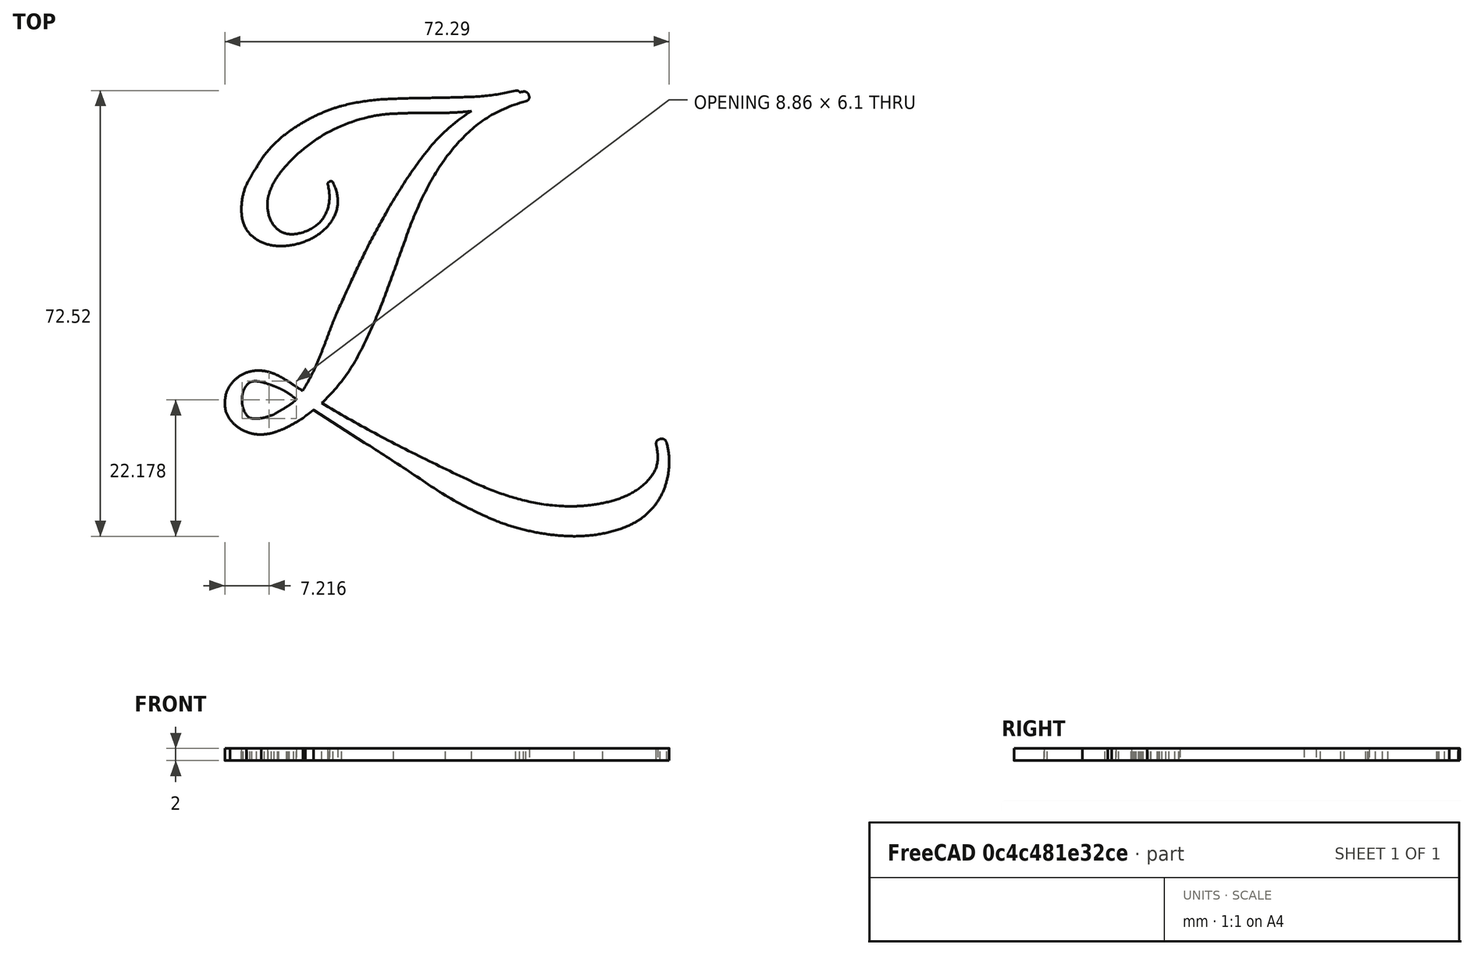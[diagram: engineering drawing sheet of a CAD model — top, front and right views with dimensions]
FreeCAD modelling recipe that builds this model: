
FCSTD DOCUMENT  (FreeCAD 0.19R24291 (Git))
Label: labritSmall
License: All rights reserved
LicenseURL: http://en.wikipedia.org/wiki/All_rights_reserved
objects: Part::Part2DObjectPython×1, Part::Extrusion×1, App::MeasureDistance×1
note: 2 computed .brp shape members not serialized (recipe doc carries the construction recipe); baked Part::Feature solids carry a one-line shape summary decoded from their .brp

FEATURE [Part::Part2DObjectPython] ShapeString  # Draft 2D object (typed FeaturePython)
  FontFile = <path> Rainbow Script FREE.ttf
  Placement = pos=(-2.3,0.7,0) rot=(0,0,1;0rad)
  Size = 25
  String = L
  Tracking = 0
FEATURE [Part::Extrusion] Extrude
  Base = -> ShapeString
  Dir = (0,0,1)
  DirMode = 2
  FaceMakerClass = Part::FaceMakerBullseye
  LengthFwd = 2
  LengthRev = 0
  Solid = false
  Symmetric = false
FEATURE [App::MeasureDistance] Distance  label="Distance: 14,98 cm"
  Distance = 149.816
  P1 = (73.2976,100.959,5)
  P2 = (138.752,-33.8018,5)
note: 1 file-system path scrubbed to <path> (originals preserved in the JSON sidecar)
